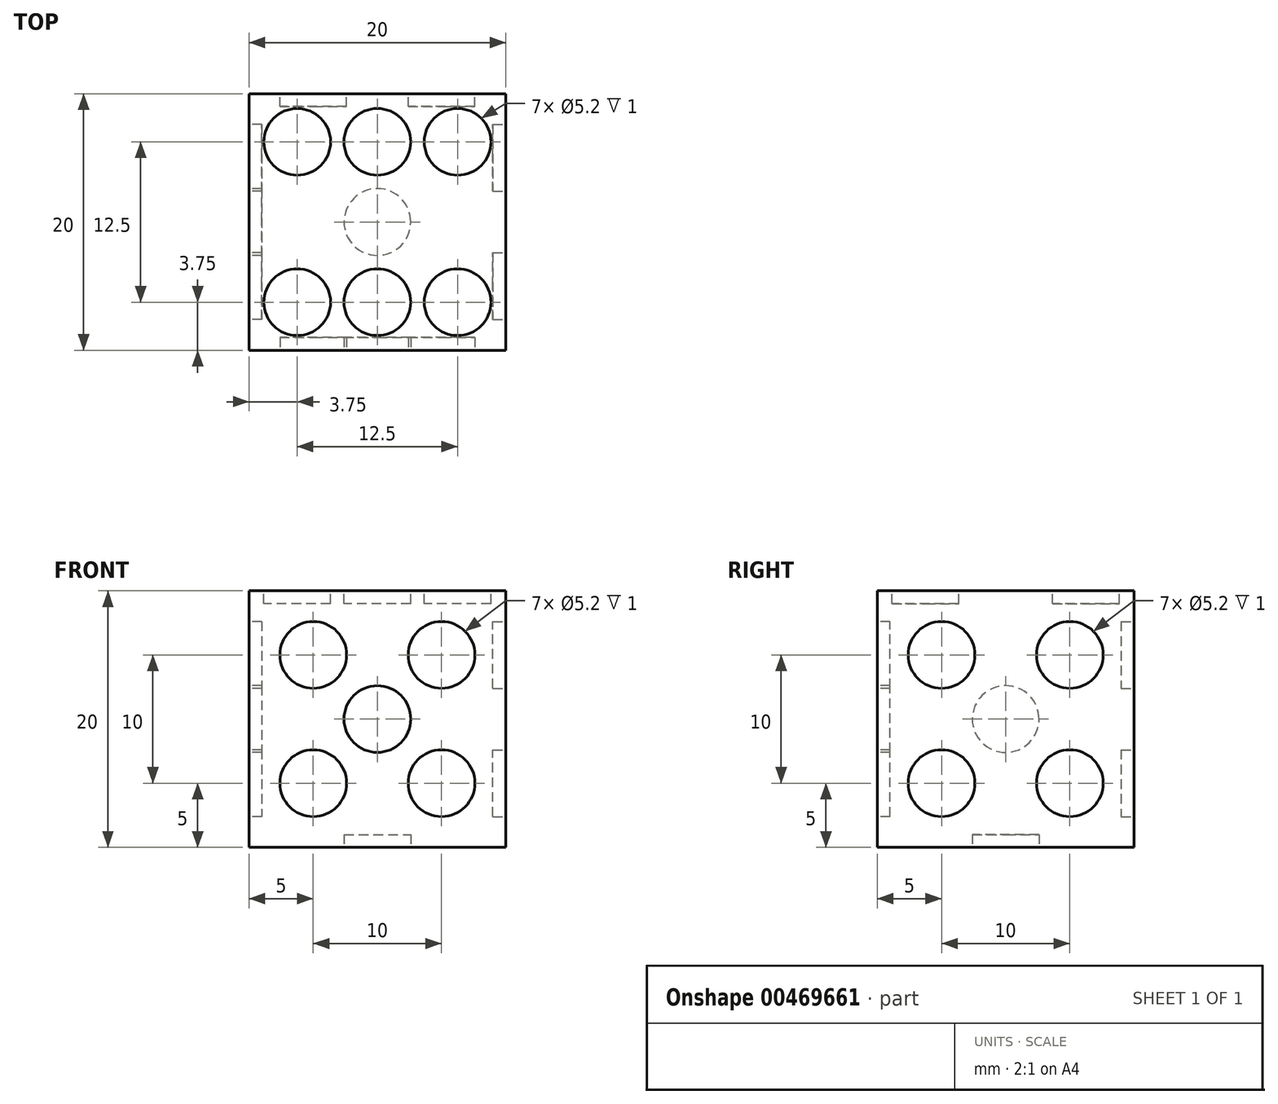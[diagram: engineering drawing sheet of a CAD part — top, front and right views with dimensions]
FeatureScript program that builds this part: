
annotation { "Feature Type Name" : "Feature", "Feature Type Description" : "" }
export const myFeature = defineFeature(function(context is Context, id is Id, definition is map)
    precondition{}
    {
        {
            var Q0;
            Q0=qCreatedBy(makeId("Front.planeOp"),FACE);
            var sketch = newSketch(context, id + "F0", { "sketchPlane" : qUnion([Q0])});
            skLineSegment(sketch, "E0.bottom", {"start": v(0, 0) * mm, "end": v(-20, 0) * mm});
            skLineSegment(sketch, "E0.top", {"start": v(0, 20) * mm, "end": v(-20, 20) * mm});
            skLineSegment(sketch, "E0.left", {"start": v(0, 0) * mm, "end": v(0, 20) * mm});
            skLineSegment(sketch, "E0.right", {"start": v(-20, 0) * mm, "end": v(-20, 20) * mm});
            skSolve(sketch);
        }
        {
            var Q0;
            Q0 = qSketchRegion(id + "F0", true);
            extrude(context, id + "F1", {"entities" : qUnion([Q0]), "depth" : 20 * mm});
        }
        {
            var Q0;
            Q0=makeQuery(id+"F1.opExtrude","CAP_FACE",FACE,{"disambiguationData":[OSD([sQuery(id+"F0.wireOp",EDGE,"E0.bottom"),sQuery(id+"F0.wireOp",EDGE,"E0.top"),sQuery(id+"F0.wireOp",EDGE,"E0.left"),sQuery(id+"F0.wireOp",EDGE,"E0.right")])],"isStart":false});
            var sketch = newSketch(context, id + "F2", { "sketchPlane" : qUnion([Q0])});
            skLineSegment(sketch, "E1", {"start": v(-10, 20) * mm, "end": v(-10, 0) * mm, "construction": true});
            skLineSegment(sketch, "E2", {"start": v(-10, 0) * mm, "end": v(0, 0) * mm, "construction": true});
            skLineSegment(sketch, "E3", {"start": v(0, 0) * mm, "end": v(0, 10) * mm, "construction": true});
            skLineSegment(sketch, "E4", {"start": v(0, 10) * mm, "end": v(-20, 10) * mm, "construction": true});
            skLineSegment(sketch, "E5", {"start": v(-20, 10) * mm, "end": v(-20, 20) * mm, "construction": true});
            skLineSegment(sketch, "E6", {"start": v(-20, 20) * mm, "end": v(0, 0) * mm, "construction": true});
            skLineSegment(sketch, "E7", {"start": v(-20, 0) * mm, "end": v(-20, 20) * mm, "construction": true});
            skLineSegment(sketch, "E8", {"start": v(0, 20) * mm, "end": v(-20, 0) * mm, "construction": true});
            skCircle(sketch, "E9", {"center": v(-10, 10) * mm, "radius": 2.6 * mm});
            skCircle(sketch, "E10", {"center": v(-15, 15) * mm, "radius": 2.6 * mm});
            skCircle(sketch, "E11.MirrorC", {"center": v(-5, 15) * mm, "radius": 2.6 * mm});
            skCircle(sketch, "E12.MirrorC", {"center": v(-15, 5) * mm, "radius": 2.6 * mm});
            skCircle(sketch, "E13.MirrorC", {"center": v(-5, 5) * mm, "radius": 2.6 * mm});
            skSolve(sketch);
        }
        {
            var Q0;
            Q0 = qSketchRegion(id + "F2", true);
            extrude(context, id + "F3", {"entities" : qUnion([Q0]), "operationType" : NewBodyOperationType.REMOVE, "oppositeDirection" : true, "depth" : 1 * mm});
        }
        {
            var Q0;
            Q0=makeQuery(id+"F1.opExtrude","SWEPT_FACE",FACE,{"disambiguationData":[OSD([sQuery(id+"F0.wireOp",EDGE,"E0.left")])]});
            var sketch = newSketch(context, id + "F4", { "sketchPlane" : qUnion([Q0])});
            skLineSegment(sketch, "E14", {"start": v(-20, 20) * mm, "end": v(-10, 20) * mm, "construction": true});
            skLineSegment(sketch, "E15", {"start": v(-10, 20) * mm, "end": v(-10, 0) * mm, "construction": true});
            skLineSegment(sketch, "E16", {"start": v(-10, 0) * mm, "end": v(-20, 0) * mm, "construction": true});
            skLineSegment(sketch, "E17", {"start": v(-20, 0) * mm, "end": v(0, 20) * mm, "construction": true});
            skLineSegment(sketch, "E18", {"start": v(0, 20) * mm, "end": v(0, 10) * mm, "construction": true});
            skLineSegment(sketch, "E19", {"start": v(0, 10) * mm, "end": v(-20, 10) * mm, "construction": true});
            skLineSegment(sketch, "E20", {"start": v(-20, 10) * mm, "end": v(-20, 20) * mm, "construction": true});
            skLineSegment(sketch, "E21", {"start": v(-20, 20) * mm, "end": v(0, 0) * mm, "construction": true});
            skCircle(sketch, "E22", {"center": v(-15, 15) * mm, "radius": 2.6 * mm});
            skCircle(sketch, "E23.MirrorC", {"center": v(-5, 15) * mm, "radius": 2.6 * mm});
            skCircle(sketch, "E24.MirrorC", {"center": v(-15, 5) * mm, "radius": 2.6 * mm});
            skCircle(sketch, "E25.MirrorC", {"center": v(-5, 5) * mm, "radius": 2.6 * mm});
            skSolve(sketch);
        }
        {
            var Q0;
            Q0 = qSketchRegion(id + "F4", true);
            extrude(context, id + "F5", {"entities" : qUnion([Q0]), "operationType" : NewBodyOperationType.REMOVE, "oppositeDirection" : true, "depth" : 1 * mm});
        }
        {
            var Q0;
            Q0=makeQuery(id+"F1.opExtrude","SWEPT_FACE",FACE,{"disambiguationData":[OSD([sQuery(id+"F0.wireOp",EDGE,"E0.right")])]});
            var sketch = newSketch(context, id + "F6", { "sketchPlane" : qUnion([Q0])});
            skLineSegment(sketch, "E26", {"start": v(0, 20) * mm, "end": v(10, 20) * mm, "construction": true});
            skLineSegment(sketch, "E27", {"start": v(10, 20) * mm, "end": v(10, 0) * mm, "construction": true});
            skLineSegment(sketch, "E28", {"start": v(10, 0) * mm, "end": v(0, 0) * mm, "construction": true});
            skLineSegment(sketch, "E29", {"start": v(0, 0) * mm, "end": v(20, 20) * mm, "construction": true});
            skLineSegment(sketch, "E30", {"start": v(20, 20) * mm, "end": v(20, 10) * mm, "construction": true});
            skLineSegment(sketch, "E31", {"start": v(20, 10) * mm, "end": v(0, 10) * mm, "construction": true});
            skLineSegment(sketch, "E32", {"start": v(0, 10) * mm, "end": v(0, 20) * mm, "construction": true});
            skLineSegment(sketch, "E33", {"start": v(0, 20) * mm, "end": v(20, 0) * mm, "construction": true});
            skCircle(sketch, "E34", {"center": v(10, 10) * mm, "radius": 2.6 * mm});
            skCircle(sketch, "E35", {"center": v(15, 15) * mm, "radius": 2.6 * mm});
            skCircle(sketch, "E36", {"center": v(5, 5) * mm, "radius": 2.6 * mm});
            skSolve(sketch);
        }
        {
            var Q0;
            Q0 = qSketchRegion(id + "F6", true);
            extrude(context, id + "F7", {"entities" : qUnion([Q0]), "operationType" : NewBodyOperationType.REMOVE, "oppositeDirection" : true, "depth" : 1 * mm});
        }
        {
            var Q0;
            Q0=makeQuery(id+"F1.opExtrude","CAP_FACE",FACE,{"disambiguationData":[OSD([sQuery(id+"F0.wireOp",EDGE,"E0.bottom"),sQuery(id+"F0.wireOp",EDGE,"E0.top"),sQuery(id+"F0.wireOp",EDGE,"E0.left"),sQuery(id+"F0.wireOp",EDGE,"E0.right")])],"isStart":true});
            var sketch = newSketch(context, id + "F8", { "sketchPlane" : qUnion([Q0])});
            skLineSegment(sketch, "E37", {"start": v(0, 20) * mm, "end": v(10, 20) * mm, "construction": true});
            skLineSegment(sketch, "E38", {"start": v(10, 20) * mm, "end": v(10, 0) * mm, "construction": true});
            skLineSegment(sketch, "E39", {"start": v(10, 0) * mm, "end": v(20, 0) * mm, "construction": true});
            skLineSegment(sketch, "E40", {"start": v(20, 0) * mm, "end": v(20, 10) * mm, "construction": true});
            skLineSegment(sketch, "E41", {"start": v(20, 10) * mm, "end": v(20, 20) * mm, "construction": true});
            skLineSegment(sketch, "E42", {"start": v(20, 20) * mm, "end": v(0, 0) * mm, "construction": true});
            skLineSegment(sketch, "E43", {"start": v(0, 0) * mm, "end": v(0, 10) * mm, "construction": true});
            skLineSegment(sketch, "E44", {"start": v(0, 10) * mm, "end": v(20, 10) * mm, "construction": true});
            skLineSegment(sketch, "E45", {"start": v(20, 0) * mm, "end": v(0, 20) * mm, "construction": true});
            skCircle(sketch, "E46", {"center": v(5, 5) * mm, "radius": 2.6 * mm});
            skCircle(sketch, "E47", {"center": v(15, 15) * mm, "radius": 2.6 * mm});
            skSolve(sketch);
        }
        {
            var Q0;
            Q0 = qSketchRegion(id + "F8", true);
            extrude(context, id + "F9", {"entities" : qUnion([Q0]), "operationType" : NewBodyOperationType.REMOVE, "oppositeDirection" : true, "depth" : 1 * mm});
        }
        {
            var Q0;
            Q0=makeQuery(id+"F1.opExtrude","SWEPT_FACE",FACE,{"disambiguationData":[OSD([sQuery(id+"F0.wireOp",EDGE,"E0.bottom")])]});
            var sketch = newSketch(context, id + "F10", { "sketchPlane" : qUnion([Q0])});
            skLineSegment(sketch, "E48", {"start": v(-20, 20) * mm, "end": v(-10, 20) * mm, "construction": true});
            skLineSegment(sketch, "E49", {"start": v(-10, 20) * mm, "end": v(-10, 0) * mm, "construction": true});
            skLineSegment(sketch, "E50", {"start": v(-10, 0) * mm, "end": v(-20, 0) * mm, "construction": true});
            skLineSegment(sketch, "E51", {"start": v(-20, 0) * mm, "end": v(0, 20) * mm, "construction": true});
            skLineSegment(sketch, "E52", {"start": v(0, 20) * mm, "end": v(0, 10) * mm, "construction": true});
            skLineSegment(sketch, "E53", {"start": v(0, 10) * mm, "end": v(-20, 10) * mm, "construction": true});
            skLineSegment(sketch, "E54", {"start": v(-20, 10) * mm, "end": v(-20, 20) * mm, "construction": true});
            skLineSegment(sketch, "E55", {"start": v(0, 0) * mm, "end": v(-20, 20) * mm, "construction": true});
            skCircle(sketch, "E56", {"center": v(-10, 10) * mm, "radius": 2.6 * mm});
            skSolve(sketch);
        }
        {
            var Q0;
            Q0 = qSketchRegion(id + "F10", true);
            extrude(context, id + "F11", {"entities" : qUnion([Q0]), "operationType" : NewBodyOperationType.REMOVE, "oppositeDirection" : true, "depth" : 1 * mm});
        }
        {
            var Q0;
            Q0=makeQuery(id+"F1.opExtrude","SWEPT_FACE",FACE,{"disambiguationData":[OSD([sQuery(id+"F0.wireOp",EDGE,"E0.top")])]});
            var sketch = newSketch(context, id + "F12", { "sketchPlane" : qUnion([Q0])});
            skLineSegment(sketch, "E57", {"start": v(0, -20) * mm, "end": v(-10, -20) * mm, "construction": true});
            skLineSegment(sketch, "E58", {"start": v(-10, -20) * mm, "end": v(-10, 0) * mm, "construction": true});
            skLineSegment(sketch, "E59", {"start": v(-10, 0) * mm, "end": v(0, 0) * mm, "construction": true});
            skLineSegment(sketch, "E60", {"start": v(0, 0) * mm, "end": v(-20, -20) * mm, "construction": true});
            skLineSegment(sketch, "E61", {"start": v(-20, -20) * mm, "end": v(-20, -10) * mm, "construction": true});
            skLineSegment(sketch, "E62", {"start": v(-20, -10) * mm, "end": v(0, -10) * mm, "construction": true});
            skLineSegment(sketch, "E63", {"start": v(0, -10) * mm, "end": v(0, -20) * mm, "construction": true});
            skLineSegment(sketch, "E64", {"start": v(-20, 0) * mm, "end": v(0, -20) * mm, "construction": true});
            skCircle(sketch, "E65", {"center": v(-3.75, -16.25) * mm, "radius": 2.6 * mm});
            skCircle(sketch, "E66.MirrorC", {"center": v(-3.75, -3.75) * mm, "radius": 2.6 * mm});
            skCircle(sketch, "E67.MirrorC", {"center": v(-16.25, -16.25) * mm, "radius": 2.6 * mm});
            skCircle(sketch, "E68.MirrorC", {"center": v(-16.25, -3.75) * mm, "radius": 2.6 * mm});
            skCircle(sketch, "E69", {"center": v(-10, -16.25) * mm, "radius": 2.6 * mm});
            skCircle(sketch, "E70.MirrorC", {"center": v(-10, -3.75) * mm, "radius": 2.6 * mm});
            skSolve(sketch);
        }
        {
            var Q0;
            Q0 = qSketchRegion(id + "F12", true);
            extrude(context, id + "F13", {"entities" : qUnion([Q0]), "operationType" : NewBodyOperationType.REMOVE, "oppositeDirection" : true, "depth" : 1 * mm});
        }
    });
